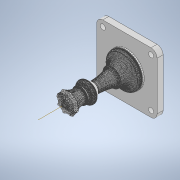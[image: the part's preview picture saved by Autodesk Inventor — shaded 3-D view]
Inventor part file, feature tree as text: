
AUTODESK INVENTOR PART (.ipt)
format: ipt  version: 2022 (Build 260153000, 153)  size: 21,519,872 bytes
history: native  units: mm
features: sketch x7, projected_geometry x4, other x3, extrude x3, move_body x2, revolve x2, hole x2, direct_edit x1, fillet x1, boolean_combine x1, sweep x1, pattern_circular x1, thicken_offset x1
ambient origin geometry x8: Origin, YZ Plane, XZ Plane, XY Plane, X Axis, Y Axis, Z Axis, Center Point
bodies: Solid1 (feature_tree), Solid2 (feature_tree), Solid3 (feature_tree), Solid4 (feature_tree)
feature tree (29):
  other  "MeshFeature1"
  direct_edit  "Direct Edit1"
  move_body  "Move Body1"
  move_body  "Move Body2"
  sketch  "Sketch1"  dims[d0=6.7mm d1=10.0mm d2=10.0mm d3=1.805mm d4=0.088mm d5=0.0mm d6=40.0mm]
  extrude  "Extrusion1"  Depth=10.0mm TaperAngle=0.0deg
  fillet  "Fillet1"  Radius=40.0mm
  extrude  "Extrusion2"  Depth=5.0mm
  boolean_combine  "Combine1"
  revolve  "Revolution1"  [1 undecoded]
  sweep  "Sweep1"
  extrude  "Extrusion3"  Depth=4.0mm TaperAngle=0.0deg
  other  "Work Axis1"
  pattern_circular  "Circular Pattern1"  Angle=90.0deg  [1 undecoded]
  thicken_offset  "Thicken1"
  hole  "Hole1"  [1 undecoded]
  hole  "Hole2"  [1 undecoded]
  revolve  "Revolution2"  [1 undecoded]
  sketch  "Sketch2"  dims[d7=0.0mm d8=-0.176mm d9=0.0mm d10=135.0deg d11=5.0mm]
  projected_geometry  "Projected Loop1"
  sketch  "Sketch3"  dims[d12=5.0mm d13=4.0mm]
  sketch  "Sketch4"  dims[d14=5.0mm d15=3.0mm]
  projected_geometry  "Projected Loop2"
  sketch  "Sketch5"  dims[d16=4.0mm d17=40.0mm d18=0.0mm]
  projected_geometry  "Projected Loop3"
  sketch  "Sketch6"  dims[d19=4.0mm]
  projected_geometry  "Projected Loop4"
  sketch  "Sketch7"  dims[d20=4.0mm d21=0.0mm d22=90.0deg d23=8.0mm d24=0.0mm d25=0.0mm d26=4.0mm d27=0.0mm d28=20.0mm d29=360.0deg d31=2.0mm d32=2.0mm d33=3.4mm d34=6.0mm d35=6.3mm d36=2.0mm d37=90.0deg d38=14.0mm d39=0.0mm d42=4.0mm d43=6.0mm d44=6.3mm d45=2.0mm d46=90.0deg d47=14.0mm d48=0.0mm d49=45.0deg d50=90.0deg]
  other  "Scale1"
note: 5 required parameter values undecoded (feature->parameter linkage not recoverable at this tier; creation-order binding heuristic only, values carry confidence <= 0.55)